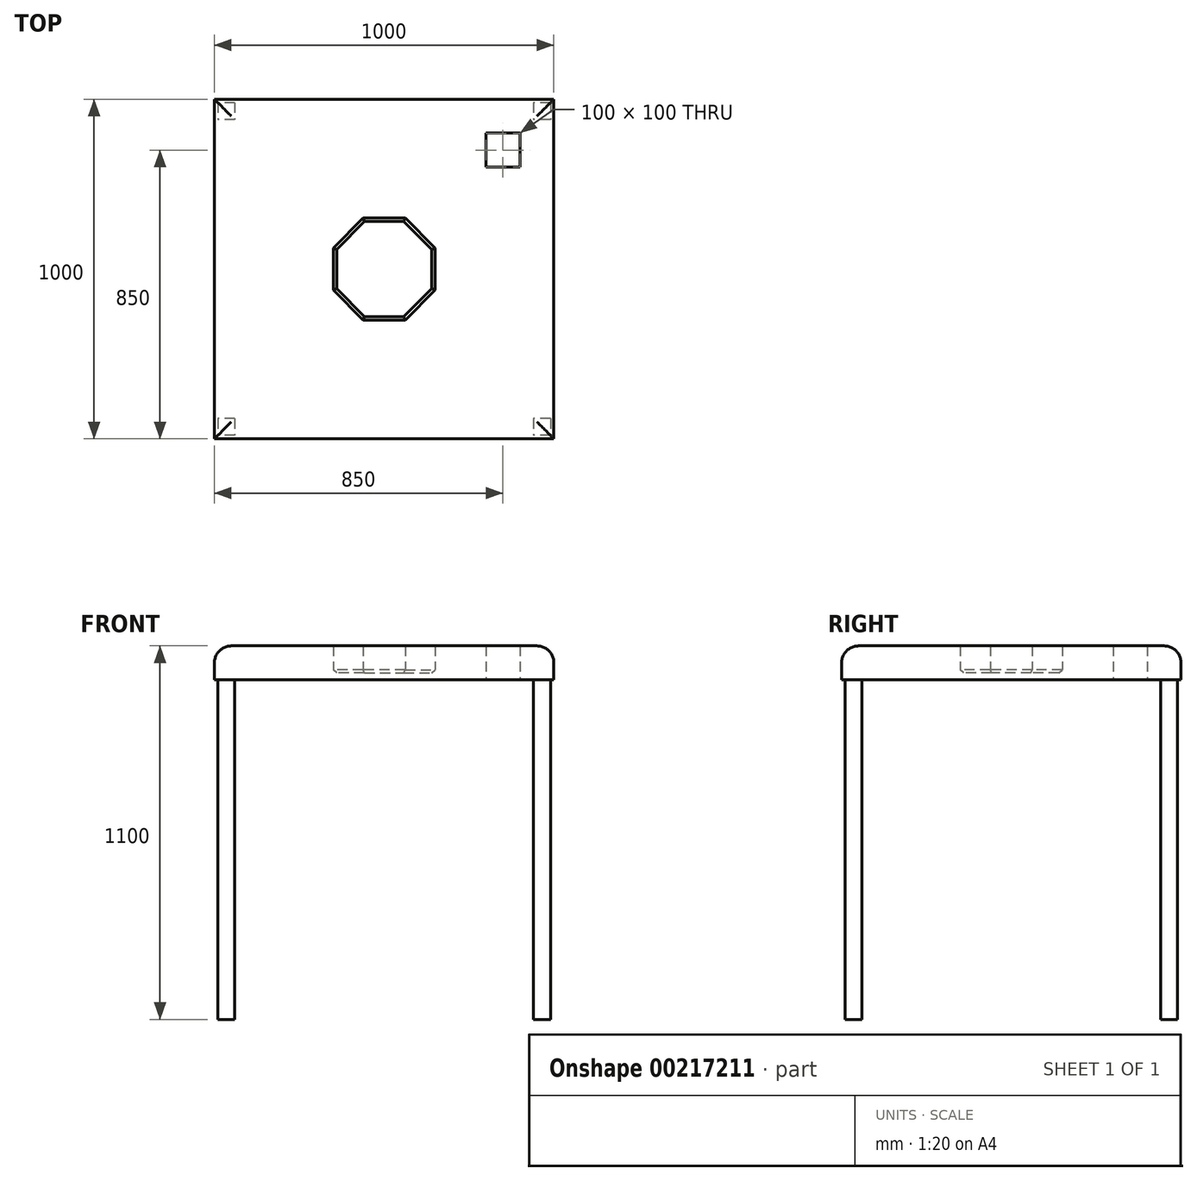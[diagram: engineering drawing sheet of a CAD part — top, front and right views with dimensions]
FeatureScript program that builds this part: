
annotation { "Feature Type Name" : "Feature", "Feature Type Description" : "" }
export const myFeature = defineFeature(function(context is Context, id is Id, definition is map)
    precondition{}
    {
        {
            var Q0;
            Q0=qCreatedBy(makeId("Top.planeOp"),FACE);
            var sketch = newSketch(context, id + "F0", { "sketchPlane" : qUnion([Q0])});
            skLineSegment(sketch, "E0.bottom", {"start": v(500, -500) * mm, "end": v(-500, -500) * mm});
            skLineSegment(sketch, "E0.top", {"start": v(500, 500) * mm, "end": v(-500, 500) * mm});
            skLineSegment(sketch, "E0.left", {"start": v(500, -500) * mm, "end": v(500, 500) * mm});
            skLineSegment(sketch, "E0.right", {"start": v(-500, -500) * mm, "end": v(-500, 500) * mm});
            skPoint(sketch, "E0.middle", {"position": v(0, 0) * mm});
            skCircle(sketch, "E1.cCircle", {"center": v(0, 0) * mm, "radius": 150 * mm, "construction": true});
            skLineSegment(sketch, "E1.0", {"start": v(150, 62.13) * mm, "end": v(150, -62.13) * mm});
            skLineSegment(sketch, "E1.1", {"start": v(150, -62.13) * mm, "end": v(62.13, -150) * mm});
            skLineSegment(sketch, "E1.2", {"start": v(62.13, -150) * mm, "end": v(-62.13, -150) * mm});
            skLineSegment(sketch, "E1.3", {"start": v(-62.13, -150) * mm, "end": v(-150, -62.13) * mm});
            skLineSegment(sketch, "E1.4", {"start": v(-150, -62.13) * mm, "end": v(-150, 62.13) * mm});
            skLineSegment(sketch, "E1.5", {"start": v(-150, 62.13) * mm, "end": v(-62.13, 150) * mm});
            skLineSegment(sketch, "E1.6", {"start": v(-62.13, 150) * mm, "end": v(62.13, 150) * mm});
            skLineSegment(sketch, "E1.7", {"start": v(62.13, 150) * mm, "end": v(150, 62.13) * mm});
            skPoint(sketch, "E1.0.midPoint", {"position": v(150, 0) * mm});
            skLineSegment(sketch, "E2.bottom", {"start": v(400, 300) * mm, "end": v(300, 300) * mm});
            skLineSegment(sketch, "E2.top", {"start": v(400, 400) * mm, "end": v(300, 400) * mm});
            skLineSegment(sketch, "E2.left", {"start": v(400, 300) * mm, "end": v(400, 400) * mm});
            skLineSegment(sketch, "E2.right", {"start": v(300, 300) * mm, "end": v(300, 400) * mm});
            skPoint(sketch, "E2.middle", {"position": v(350, 350) * mm});
            skSolve(sketch);
        }
        {
            var Q0;
            Q0=makeQuery(id+"F0.imprint","IMPRINT",FACE,{"disambiguationData":[TD([[makeQuery(id+"F0.imprint","IMPRINT",EDGE,{"derivedFrom":sQuery(id+"F0.wireOp",EDGE,"E0.bottom")}),-1.0]])]});
            extrude(context, id + "F1", {"entities" : qUnion([Q0]), "depth" : 100 * mm});
        }
        {
            var Q0;
            Q0=makeQuery(id+"F1.opExtrude","CAP_EDGE",EDGE,{"disambiguationData":[OSD([sQuery(id+"F0.wireOp",EDGE,"E0.bottom")])],"isStart":false});
            var Q1;
            Q1=makeQuery(id+"F1.opExtrude","CAP_EDGE",EDGE,{"disambiguationData":[OSD([sQuery(id+"F0.wireOp",EDGE,"E0.right")])],"isStart":false});
            var Q2;
            Q2=makeQuery(id+"F1.opExtrude","CAP_EDGE",EDGE,{"disambiguationData":[OSD([sQuery(id+"F0.wireOp",EDGE,"E0.top")])],"isStart":false});
            var Q3;
            Q3=makeQuery(id+"F1.opExtrude","CAP_EDGE",EDGE,{"disambiguationData":[OSD([sQuery(id+"F0.wireOp",EDGE,"E0.left")])],"isStart":false});
            fillet(context, id + "F2", {"entities" : qUnion([Q0, Q1, Q2, Q3]), "radius" : 50 * mm, "tangentPropagation" : true, "allowEdgeOverflow" : false});
        }
        {
            var Q0;
            Q0=makeQuery(id+"F1.opExtrude","CAP_FACE",FACE,{"disambiguationData":[OSD([sQuery(id+"F0.wireOp",EDGE,"E0.bottom"),sQuery(id+"F0.wireOp",EDGE,"E0.top"),sQuery(id+"F0.wireOp",EDGE,"E0.left"),sQuery(id+"F0.wireOp",EDGE,"E0.right"),sQuery(id+"F0.wireOp",EDGE,"E1.0"),sQuery(id+"F0.wireOp",EDGE,"E1.1"),sQuery(id+"F0.wireOp",EDGE,"E1.2"),sQuery(id+"F0.wireOp",EDGE,"E1.3"),sQuery(id+"F0.wireOp",EDGE,"E1.4"),sQuery(id+"F0.wireOp",EDGE,"E1.5"),sQuery(id+"F0.wireOp",EDGE,"E1.6"),sQuery(id+"F0.wireOp",EDGE,"E1.7"),sQuery(id+"F0.wireOp",EDGE,"E2.bottom"),sQuery(id+"F0.wireOp",EDGE,"E2.top"),sQuery(id+"F0.wireOp",EDGE,"E2.left"),sQuery(id+"F0.wireOp",EDGE,"E2.right")])],"isStart":true});
            var sketch = newSketch(context, id + "F3", { "sketchPlane" : qUnion([Q0])});
            skCircle(sketch, "E3.cCircle", {"center": v(0, 0) * mm, "radius": 150 * mm, "construction": true});
            skLineSegment(sketch, "E3.0", {"start": v(150, 62.13) * mm, "end": v(150, -62.13) * mm});
            skLineSegment(sketch, "E3.1", {"start": v(150, -62.13) * mm, "end": v(62.13, -150) * mm});
            skLineSegment(sketch, "E3.2", {"start": v(62.13, -150) * mm, "end": v(-62.13, -150) * mm});
            skLineSegment(sketch, "E3.3", {"start": v(-62.13, -150) * mm, "end": v(-150, -62.13) * mm});
            skLineSegment(sketch, "E3.4", {"start": v(-150, -62.13) * mm, "end": v(-150, 62.13) * mm});
            skLineSegment(sketch, "E3.5", {"start": v(-150, 62.13) * mm, "end": v(-62.13, 150) * mm});
            skLineSegment(sketch, "E3.6", {"start": v(-62.13, 150) * mm, "end": v(62.13, 150) * mm});
            skLineSegment(sketch, "E3.7", {"start": v(62.13, 150) * mm, "end": v(150, 62.13) * mm});
            skPoint(sketch, "E3.0.midPoint", {"position": v(150, 0) * mm});
            skSolve(sketch);
        }
        {
            var Q0;
            Q0 = qSketchRegion(id + "F3", true);
            extrude(context, id + "F4", {"entities" : qUnion([Q0]), "operationType" : NewBodyOperationType.ADD, "oppositeDirection" : true, "depth" : 20 * mm});
        }
        {
            var Q0;
            Q0=makeQuery(id+"F4.boolean.opBoolean","MERGE",FACE,{"derivedFrom":[makeQuery(id+"F1.opExtrude","CAP_FACE",FACE,{"disambiguationData":[OSD([sQuery(id+"F0.wireOp",EDGE,"E0.bottom"),sQuery(id+"F0.wireOp",EDGE,"E0.top"),sQuery(id+"F0.wireOp",EDGE,"E0.left"),sQuery(id+"F0.wireOp",EDGE,"E0.right"),sQuery(id+"F0.wireOp",EDGE,"E1.0"),sQuery(id+"F0.wireOp",EDGE,"E1.1"),sQuery(id+"F0.wireOp",EDGE,"E1.2"),sQuery(id+"F0.wireOp",EDGE,"E1.3"),sQuery(id+"F0.wireOp",EDGE,"E1.4"),sQuery(id+"F0.wireOp",EDGE,"E1.5"),sQuery(id+"F0.wireOp",EDGE,"E1.6"),sQuery(id+"F0.wireOp",EDGE,"E1.7"),sQuery(id+"F0.wireOp",EDGE,"E2.bottom"),sQuery(id+"F0.wireOp",EDGE,"E2.top"),sQuery(id+"F0.wireOp",EDGE,"E2.left"),sQuery(id+"F0.wireOp",EDGE,"E2.right")])],"isStart":true}),makeQuery(id+"F4.opExtrude","CAP_FACE",FACE,{"disambiguationData":[OSD([sQuery(id+"F3.wireOp",EDGE,"E3.0"),sQuery(id+"F3.wireOp",EDGE,"E3.1"),sQuery(id+"F3.wireOp",EDGE,"E3.2"),sQuery(id+"F3.wireOp",EDGE,"E3.3"),sQuery(id+"F3.wireOp",EDGE,"E3.4"),sQuery(id+"F3.wireOp",EDGE,"E3.5"),sQuery(id+"F3.wireOp",EDGE,"E3.6"),sQuery(id+"F3.wireOp",EDGE,"E3.7")])],"isStart":true})]});
            var sketch = newSketch(context, id + "F5", { "sketchPlane" : qUnion([Q0])});
            skLineSegment(sketch, "E4.bottom", {"start": v(-440, 440) * mm, "end": v(-490, 440) * mm});
            skLineSegment(sketch, "E4.top", {"start": v(-440, 490) * mm, "end": v(-490, 490) * mm});
            skLineSegment(sketch, "E4.left", {"start": v(-440, 440) * mm, "end": v(-440, 490) * mm});
            skLineSegment(sketch, "E4.right", {"start": v(-490, 440) * mm, "end": v(-490, 490) * mm});
            skPoint(sketch, "E4.middle", {"position": v(-465, 465) * mm});
            skLineSegment(sketch, "E5.bottom", {"start": v(-440, -490) * mm, "end": v(-490, -490) * mm});
            skLineSegment(sketch, "E5.top", {"start": v(-440, -440) * mm, "end": v(-490, -440) * mm});
            skLineSegment(sketch, "E5.left", {"start": v(-440, -490) * mm, "end": v(-440, -440) * mm});
            skLineSegment(sketch, "E5.right", {"start": v(-490, -490) * mm, "end": v(-490, -440) * mm});
            skLineSegment(sketch, "E6.bottom", {"start": v(490, -490) * mm, "end": v(440, -490) * mm});
            skLineSegment(sketch, "E6.top", {"start": v(490, -440) * mm, "end": v(440, -440) * mm});
            skLineSegment(sketch, "E6.left", {"start": v(490, -490) * mm, "end": v(490, -440) * mm});
            skLineSegment(sketch, "E6.right", {"start": v(440, -490) * mm, "end": v(440, -440) * mm});
            skLineSegment(sketch, "E7.bottom", {"start": v(490, 440) * mm, "end": v(440, 440) * mm});
            skLineSegment(sketch, "E7.top", {"start": v(490, 490) * mm, "end": v(440, 490) * mm});
            skLineSegment(sketch, "E7.left", {"start": v(490, 440) * mm, "end": v(490, 490) * mm});
            skLineSegment(sketch, "E7.right", {"start": v(440, 440) * mm, "end": v(440, 490) * mm});
            skSolve(sketch);
        }
        {
            var Q0;
            Q0 = qSketchRegion(id + "F5", true);
            extrude(context, id + "F6", {"entities" : qUnion([Q0]), "operationType" : NewBodyOperationType.ADD, "depth" : 1000 * mm});
        }
        {
            var Q0;
            Q0=makeQuery(id+"F4.opExtrude","CAP_FACE",FACE,{"disambiguationData":[OSD([sQuery(id+"F3.wireOp",EDGE,"E3.0"),sQuery(id+"F3.wireOp",EDGE,"E3.1"),sQuery(id+"F3.wireOp",EDGE,"E3.2"),sQuery(id+"F3.wireOp",EDGE,"E3.3"),sQuery(id+"F3.wireOp",EDGE,"E3.4"),sQuery(id+"F3.wireOp",EDGE,"E3.5"),sQuery(id+"F3.wireOp",EDGE,"E3.6"),sQuery(id+"F3.wireOp",EDGE,"E3.7")])],"isStart":false});
            chamfer(context, id + "F7", {"entities" : qUnion([Q0]), "width" : 10 * mm, "tangentPropagation" : true});
        }
    });
